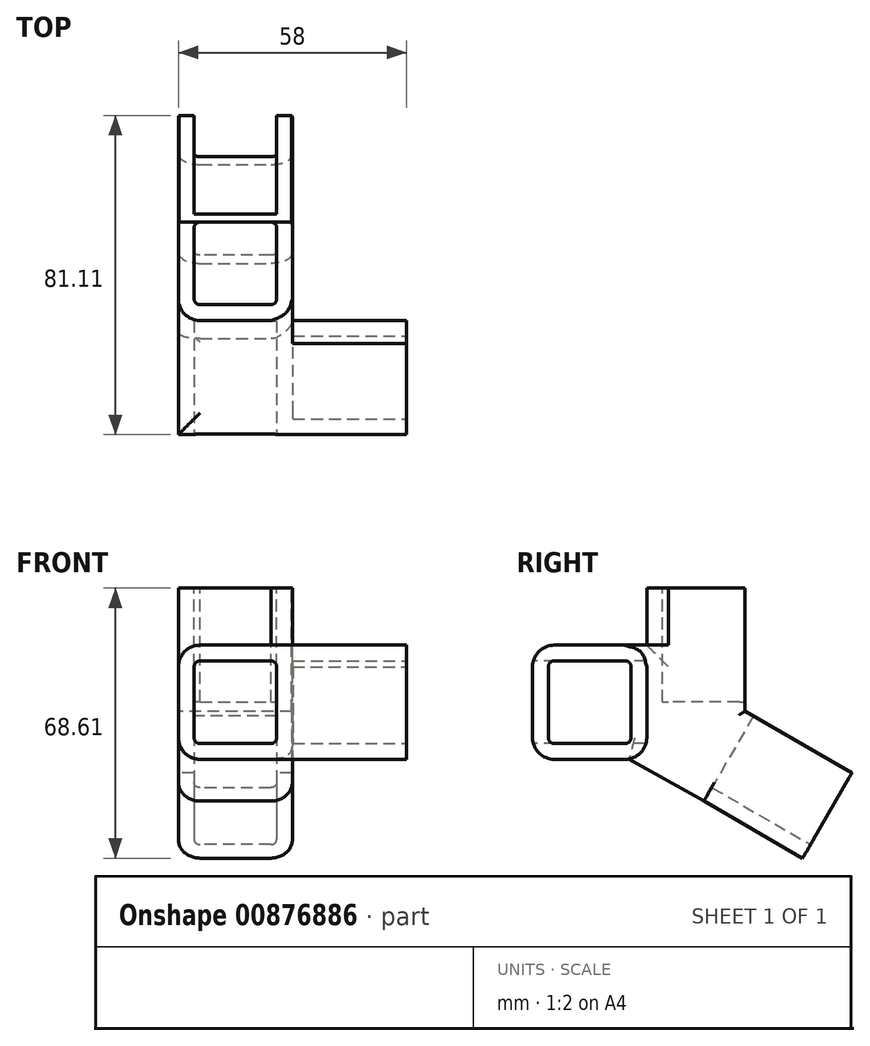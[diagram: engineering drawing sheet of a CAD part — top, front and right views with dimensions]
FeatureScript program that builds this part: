
annotation { "Feature Type Name" : "Feature", "Feature Type Description" : "" }
export const myFeature = defineFeature(function(context is Context, id is Id, definition is map)
    precondition{}
    {
        {
            var Q0;
            Q0=qCreatedBy(makeId("Front.planeOp"),FACE);
            var sketch = newSketch(context, id + "F0", { "sketchPlane" : qUnion([Q0])});
            skLineSegment(sketch, "E0.bottom", {"start": v(-21.09, 20.47) * mm, "end": v(36.91, 20.47) * mm});
            skLineSegment(sketch, "E0.top", {"start": v(-21.09, -8.53) * mm, "end": v(36.91, -8.53) * mm});
            skLineSegment(sketch, "E0.left", {"start": v(-21.09, 20.47) * mm, "end": v(-21.09, -8.53) * mm});
            skLineSegment(sketch, "E0.right", {"start": v(36.91, 20.47) * mm, "end": v(36.91, -8.53) * mm});
            skSolve(sketch);
        }
        {
            var Q0;
            Q0=makeQuery(id+"F0.imprint","IMPRINT",FACE,{"disambiguationData":[TD([[makeQuery(id+"F0.imprint","IMPRINT",EDGE,{"derivedFrom":sQuery(id+"F0.wireOp",EDGE,"E0.bottom")}),-1.0]])]});
            extrude(context, id + "F1", {"entities" : qUnion([Q0]), "depth" : 29 * mm, "offsetDistance" : 25 * mm});
        }
        {
            var Q0;
            Q0=makeQuery(id+"F1.opExtrude","CAP_FACE",FACE,{"disambiguationData":[OSD([sQuery(id+"F0.wireOp",EDGE,"E0.bottom"),sQuery(id+"F0.wireOp",EDGE,"E0.top"),sQuery(id+"F0.wireOp",EDGE,"E0.left"),sQuery(id+"F0.wireOp",EDGE,"E0.right")])],"isStart":false});
            var sketch = newSketch(context, id + "F2", { "sketchPlane" : qUnion([Q0])});
            skLineSegment(sketch, "E1.bottom", {"start": v(-17.09, 16.47) * mm, "end": v(3.91, 16.47) * mm});
            skLineSegment(sketch, "E1.top", {"start": v(-17.09, -4.53) * mm, "end": v(3.91, -4.53) * mm});
            skLineSegment(sketch, "E1.left", {"start": v(-17.09, 16.47) * mm, "end": v(-17.09, -4.53) * mm});
            skLineSegment(sketch, "E1.right", {"start": v(3.91, 16.47) * mm, "end": v(3.91, -4.53) * mm});
            skSolve(sketch);
        }
        {
            var Q0;
            Q0=makeQuery(id+"F2.imprint","IMPRINT",FACE,{"disambiguationData":[TD([[makeQuery(id+"F2.imprint","IMPRINT",EDGE,{"derivedFrom":sQuery(id+"F2.wireOp",EDGE,"E1.bottom")}),-1.0]])]});
            extrude(context, id + "F3", {"entities" : qUnion([Q0]), "operationType" : NewBodyOperationType.REMOVE, "oppositeDirection" : true, "depth" : 28.9 * mm, "offsetDistance" : 25 * mm});
        }
        {
            var Q0;
            Q0=makeQuery(id+"F1.opExtrude","SWEPT_FACE",FACE,{"disambiguationData":[OSD([sQuery(id+"F0.wireOp",EDGE,"E0.right")])]});
            var sketch = newSketch(context, id + "F4", { "sketchPlane" : qUnion([Q0])});
            skLineSegment(sketch, "E2.bottom", {"start": v(-25, 16.47) * mm, "end": v(-4, 16.47) * mm});
            skLineSegment(sketch, "E2.top", {"start": v(-25, -4.53) * mm, "end": v(-4, -4.53) * mm});
            skLineSegment(sketch, "E2.left", {"start": v(-25, 16.47) * mm, "end": v(-25, -4.53) * mm});
            skLineSegment(sketch, "E2.right", {"start": v(-4, 16.47) * mm, "end": v(-4, -4.53) * mm});
            skSolve(sketch);
        }
        {
            var Q0;
            Q0=makeQuery(id+"F4.imprint","IMPRINT",FACE,{"disambiguationData":[TD([[makeQuery(id+"F4.imprint","IMPRINT",EDGE,{"derivedFrom":sQuery(id+"F4.wireOp",EDGE,"E2.bottom")}),-1.0]])]});
            extrude(context, id + "F5", {"entities" : qUnion([Q0]), "operationType" : NewBodyOperationType.REMOVE, "oppositeDirection" : true, "depth" : 28.9 * mm, "offsetDistance" : 25 * mm});
        }
        {
            var Q0;
            Q0=makeQuery(id+"F1.opExtrude","SWEPT_FACE",FACE,{"disambiguationData":[OSD([sQuery(id+"F0.wireOp",EDGE,"E0.bottom")])]});
            var sketch = newSketch(context, id + "F6", { "sketchPlane" : qUnion([Q0])});
            skLineSegment(sketch, "E3.bottom", {"start": v(-21.09, 0) * mm, "end": v(7.91, 0) * mm});
            skLineSegment(sketch, "E3.top", {"start": v(-21.09, 29) * mm, "end": v(7.91, 29) * mm});
            skLineSegment(sketch, "E3.left", {"start": v(-21.09, 0) * mm, "end": v(-21.09, 29) * mm});
            skLineSegment(sketch, "E3.right", {"start": v(7.91, 0) * mm, "end": v(7.91, 29) * mm});
            skSolve(sketch);
        }
        {
            var Q0;
            Q0=makeQuery(id+"F6.imprint","IMPRINT",FACE,{"disambiguationData":[TD([[makeQuery(id+"F6.imprint","IMPRINT",EDGE,{"derivedFrom":sQuery(id+"F6.wireOp",EDGE,"E3.bottom")}),1.0]])]});
            extrude(context, id + "F7", {"entities" : qUnion([Q0]), "operationType" : NewBodyOperationType.ADD, "oppositeDirection" : true, "depth" : 14.5 * mm, "offsetDistance" : 25 * mm});
        }
        {
            var Q0;
            Q0=makeQuery(id+"F7.boolean.opBoolean","MERGE",FACE,{"derivedFrom":[makeQuery(id+"F1.opExtrude","SWEPT_FACE",FACE,{"disambiguationData":[OSD([sQuery(id+"F0.wireOp",EDGE,"E0.bottom")])]}),makeQuery(id+"F7.opExtrude","CAP_FACE",FACE,{"disambiguationData":[OSD([sQuery(id+"F6.wireOp",EDGE,"E3.bottom"),sQuery(id+"F6.wireOp",EDGE,"E3.top"),sQuery(id+"F6.wireOp",EDGE,"E3.left"),sQuery(id+"F6.wireOp",EDGE,"E3.right")])],"isStart":true})]});
            var sketch = newSketch(context, id + "F8", { "sketchPlane" : qUnion([Q0])});
            skLineSegment(sketch, "E4.bottom", {"start": v(-21.09, 29) * mm, "end": v(7.91, 29) * mm});
            skLineSegment(sketch, "E4.top", {"start": v(-21.09, 0) * mm, "end": v(7.91, 0) * mm});
            skLineSegment(sketch, "E4.left", {"start": v(-21.09, 29) * mm, "end": v(-21.09, 0) * mm});
            skLineSegment(sketch, "E4.right", {"start": v(7.91, 29) * mm, "end": v(7.91, 0) * mm});
            skSolve(sketch);
        }
        {
            var Q0;
            Q0=makeQuery(id+"F8.imprint","IMPRINT",FACE,{"disambiguationData":[TD([[makeQuery(id+"F8.imprint","IMPRINT",EDGE,{"derivedFrom":sQuery(id+"F8.wireOp",EDGE,"E4.bottom")}),-1.0]])]});
            extrude(context, id + "F9", {"entities" : qUnion([Q0]), "operationType" : NewBodyOperationType.ADD, "depth" : 14.5 * mm, "offsetDistance" : 25 * mm});
        }
        {
            var Q0;
            Q0=makeQuery(id+"F9.opExtrude","CAP_FACE",FACE,{"disambiguationData":[OSD([sQuery(id+"F8.wireOp",EDGE,"E4.bottom"),sQuery(id+"F8.wireOp",EDGE,"E4.top"),sQuery(id+"F8.wireOp",EDGE,"E4.left"),sQuery(id+"F8.wireOp",EDGE,"E4.right")])],"isStart":false});
            var sketch = newSketch(context, id + "F10", { "sketchPlane" : qUnion([Q0])});
            skLineSegment(sketch, "E5.bottom", {"start": v(-17.09, 25) * mm, "end": v(3.91, 25) * mm});
            skLineSegment(sketch, "E5.top", {"start": v(-17.09, 4) * mm, "end": v(3.91, 4) * mm});
            skLineSegment(sketch, "E5.left", {"start": v(-17.09, 25) * mm, "end": v(-17.09, 4) * mm});
            skLineSegment(sketch, "E5.right", {"start": v(3.91, 25) * mm, "end": v(3.91, 4) * mm});
            skSolve(sketch);
        }
        {
            var Q0;
            Q0=makeQuery(id+"F10.imprint","IMPRINT",FACE,{"disambiguationData":[TD([[makeQuery(id+"F10.imprint","IMPRINT",EDGE,{"derivedFrom":sQuery(id+"F10.wireOp",EDGE,"E5.bottom")}),-1.0]])]});
            extrude(context, id + "F11", {"entities" : qUnion([Q0]), "operationType" : NewBodyOperationType.REMOVE, "oppositeDirection" : true, "depth" : 28.9 * mm, "offsetDistance" : 25 * mm});
        }
        {
            var Q0;
            Q0=makeQuery(id+"F9.boolean.opBoolean","MERGE",FACE,{"derivedFrom":[makeQuery(id+"F7.opExtrude","SWEPT_FACE",FACE,{"disambiguationData":[OSD([sQuery(id+"F6.wireOp",EDGE,"E3.right")])]}),makeQuery(id+"F9.opExtrude","SWEPT_FACE",FACE,{"disambiguationData":[OSD([sQuery(id+"F8.wireOp",EDGE,"E4.right")])]})]});
            var sketch = newSketch(context, id + "F12", { "sketchPlane" : qUnion([Q0])});
            skLineSegment(sketch, "E6", {"start": v(29, 5.97) * mm, "end": v(54.11, -8.53) * mm});
            skLineSegment(sketch, "E7", {"start": v(54.11, -8.53) * mm, "end": v(39.61, -33.64) * mm});
            skLineSegment(sketch, "E8", {"start": v(39.61, -33.64) * mm, "end": v(14.5, -19.14) * mm});
            skLineSegment(sketch, "E9", {"start": v(14.5, -19.14) * mm, "end": v(29, 5.97) * mm});
            skLineSegment(sketch, "E10", {"start": v(14.5, -19.14) * mm, "end": v(-4.5, -8.53) * mm});
            skLineSegment(sketch, "E11", {"start": v(-4.5, -8.53) * mm, "end": v(0, -8.53) * mm});
            skLineSegment(sketch, "E12", {"start": v(0, -8.53) * mm, "end": v(0, 5.97) * mm});
            skLineSegment(sketch, "E13", {"start": v(0, 5.97) * mm, "end": v(29, 5.97) * mm});
            skSolve(sketch);
        }
        {
            var Q0;
            Q0=makeQuery(id+"F12.imprint","IMPRINT",FACE,{"disambiguationData":[TD([[makeQuery(id+"F12.imprint","IMPRINT",EDGE,{"derivedFrom":sQuery(id+"F12.wireOp",EDGE,"E6")}),-1.0]])]});
            var Q1;
            Q1=makeQuery(id+"F12.imprint","IMPRINT",FACE,{"disambiguationData":[TD([[makeQuery(id+"F12.imprint","IMPRINT",EDGE,{"derivedFrom":sQuery(id+"F12.wireOp",EDGE,"E9")}),1.0]])]});
            extrude(context, id + "F13", {"entities" : qUnion([Q0, Q1]), "operationType" : NewBodyOperationType.ADD, "oppositeDirection" : true, "depth" : 29 * mm, "offsetDistance" : 25 * mm});
        }
        {
            var Q0;
            Q0=makeQuery(id+"F13.opExtrude","SWEPT_FACE",FACE,{"disambiguationData":[OSD([sQuery(id+"F12.wireOp",EDGE,"E7")])]});
            var sketch = newSketch(context, id + "F14", { "sketchPlane" : qUnion([Q0])});
            skLineSegment(sketch, "E14.bottom", {"start": v(-3.91, 15.67) * mm, "end": v(17.09, 15.67) * mm});
            skLineSegment(sketch, "E14.top", {"start": v(-3.91, -5.33) * mm, "end": v(17.09, -5.33) * mm});
            skLineSegment(sketch, "E14.left", {"start": v(-3.91, 15.67) * mm, "end": v(-3.91, -5.33) * mm});
            skLineSegment(sketch, "E14.right", {"start": v(17.09, 15.67) * mm, "end": v(17.09, -5.33) * mm});
            skSolve(sketch);
        }
        {
            var Q0;
            Q0=makeQuery(id+"F14.imprint","IMPRINT",FACE,{"disambiguationData":[TD([[makeQuery(id+"F14.imprint","IMPRINT",EDGE,{"derivedFrom":sQuery(id+"F14.wireOp",EDGE,"E14.bottom")}),-1.0]])]});
            extrude(context, id + "F15", {"entities" : qUnion([Q0]), "operationType" : NewBodyOperationType.REMOVE, "oppositeDirection" : true, "depth" : 28.9 * mm, "offsetDistance" : 25 * mm});
        }
        {
            var Q0;
            Q0=makeQuery(id+"F15.boolean.opBoolean","COPY",EDGE,{"derivedFrom":makeQuery(id+"F15.opExtrude","SWEPT_EDGE",EDGE,{"disambiguationData":[OSD([sQuery(id+"F14.wireOp",EDGE,"E14.top"),sQuery(id+"F14.wireOp",EDGE,"E14.left")])]})});
            var Q1;
            Q1=makeQuery(id+"F15.boolean.opBoolean","COPY",EDGE,{"derivedFrom":makeQuery(id+"F15.opExtrude","SWEPT_EDGE",EDGE,{"disambiguationData":[OSD([sQuery(id+"F14.wireOp",EDGE,"E14.top"),sQuery(id+"F14.wireOp",EDGE,"E14.right")])]})});
            var Q2;
            Q2=makeQuery(id+"F11.boolean.opBoolean","COPY",EDGE,{"derivedFrom":makeQuery(id+"F11.opExtrude","SWEPT_EDGE",EDGE,{"disambiguationData":[OSD([sQuery(id+"F10.wireOp",EDGE,"E5.bottom"),sQuery(id+"F10.wireOp",EDGE,"E5.right")])]})});
            var Q3;
            Q3=makeQuery(id+"F11.boolean.opBoolean","COPY",EDGE,{"derivedFrom":makeQuery(id+"F11.opExtrude","SWEPT_EDGE",EDGE,{"disambiguationData":[OSD([sQuery(id+"F10.wireOp",EDGE,"E5.bottom"),sQuery(id+"F10.wireOp",EDGE,"E5.left")])]})});
            var Q4;
            Q4=makeQuery(id+"F11.boolean.opBoolean","COPY",EDGE,{"derivedFrom":makeQuery(id+"F11.opExtrude","SWEPT_EDGE",EDGE,{"disambiguationData":[OSD([sQuery(id+"F10.wireOp",EDGE,"E5.top"),sQuery(id+"F10.wireOp",EDGE,"E5.left")])]})});
            var Q5;
            Q5=makeQuery(id+"F11.boolean.opBoolean","COPY",EDGE,{"derivedFrom":makeQuery(id+"F11.opExtrude","SWEPT_EDGE",EDGE,{"disambiguationData":[OSD([sQuery(id+"F10.wireOp",EDGE,"E5.top"),sQuery(id+"F10.wireOp",EDGE,"E5.right")])]})});
            var Q6;
            Q6=makeQuery(id+"F5.boolean.opBoolean","COPY",EDGE,{"derivedFrom":makeQuery(id+"F5.opExtrude","SWEPT_EDGE",EDGE,{"disambiguationData":[OSD([sQuery(id+"F4.wireOp",EDGE,"E2.top"),sQuery(id+"F4.wireOp",EDGE,"E2.right")])]})});
            var Q7;
            Q7=makeQuery(id+"F5.boolean.opBoolean","COPY",EDGE,{"derivedFrom":makeQuery(id+"F5.opExtrude","SWEPT_EDGE",EDGE,{"disambiguationData":[OSD([sQuery(id+"F4.wireOp",EDGE,"E2.bottom"),sQuery(id+"F4.wireOp",EDGE,"E2.right")])]})});
            var Q8;
            Q8=makeQuery(id+"F5.boolean.opBoolean","COPY",EDGE,{"derivedFrom":makeQuery(id+"F5.opExtrude","SWEPT_EDGE",EDGE,{"disambiguationData":[OSD([sQuery(id+"F4.wireOp",EDGE,"E2.bottom"),sQuery(id+"F4.wireOp",EDGE,"E2.left")])]})});
            var Q9;
            Q9=makeQuery(id+"F5.boolean.opBoolean","COPY",EDGE,{"derivedFrom":makeQuery(id+"F5.opExtrude","SWEPT_EDGE",EDGE,{"disambiguationData":[OSD([sQuery(id+"F4.wireOp",EDGE,"E2.top"),sQuery(id+"F4.wireOp",EDGE,"E2.left")])]})});
            var Q10;
            Q10=makeQuery(id+"F3.boolean.opBoolean","COPY",EDGE,{"derivedFrom":makeQuery(id+"F3.opExtrude","SWEPT_EDGE",EDGE,{"disambiguationData":[OSD([sQuery(id+"F2.wireOp",EDGE,"E1.bottom"),sQuery(id+"F2.wireOp",EDGE,"E1.right")])]})});
            var Q11;
            Q11=makeQuery(id+"F3.boolean.opBoolean","COPY",EDGE,{"derivedFrom":makeQuery(id+"F3.opExtrude","SWEPT_EDGE",EDGE,{"disambiguationData":[OSD([sQuery(id+"F2.wireOp",EDGE,"E1.bottom"),sQuery(id+"F2.wireOp",EDGE,"E1.left")])]})});
            var Q12;
            Q12=makeQuery(id+"F3.boolean.opBoolean","COPY",EDGE,{"derivedFrom":makeQuery(id+"F3.opExtrude","SWEPT_EDGE",EDGE,{"disambiguationData":[OSD([sQuery(id+"F2.wireOp",EDGE,"E1.top"),sQuery(id+"F2.wireOp",EDGE,"E1.left")])]})});
            var Q13;
            Q13=makeQuery(id+"F3.boolean.opBoolean","COPY",EDGE,{"derivedFrom":makeQuery(id+"F3.opExtrude","SWEPT_EDGE",EDGE,{"disambiguationData":[OSD([sQuery(id+"F2.wireOp",EDGE,"E1.top"),sQuery(id+"F2.wireOp",EDGE,"E1.right")])]})});
            fillet(context, id + "F16", {"entities" : qUnion([Q0, Q1, Q2, Q3, Q4, Q5, Q6, Q7, Q8, Q9, Q10, Q11, Q12, Q13]), "radius" : 1.5 * mm, "tangentPropagation" : true, "allowEdgeOverflow" : false});
        }
        {
            var Q0;
            Q0=makeQuery(id+"F9.boolean.opBoolean","MERGE",EDGE,{"derivedFrom":[makeQuery(id+"F7.opExtrude","SWEPT_EDGE",EDGE,{"disambiguationData":[OSD([sQuery(id+"F6.wireOp",EDGE,"E3.top"),sQuery(id+"F6.wireOp",EDGE,"E3.right")])]}),makeQuery(id+"F9.opExtrude","SWEPT_EDGE",EDGE,{"disambiguationData":[OSD([sQuery(id+"F8.wireOp",EDGE,"E4.bottom"),sQuery(id+"F8.wireOp",EDGE,"E4.right")])]})]});
            var Q1;
            Q1=makeQuery(id+"F9.boolean.opBoolean","MERGE",EDGE,{"derivedFrom":[makeQuery(id+"F7.opExtrude","SWEPT_EDGE",EDGE,{"disambiguationData":[OSD([sQuery(id+"F6.wireOp",EDGE,"E3.top"),sQuery(id+"F6.wireOp",EDGE,"E3.left")])]}),makeQuery(id+"F9.opExtrude","SWEPT_EDGE",EDGE,{"disambiguationData":[OSD([sQuery(id+"F8.wireOp",EDGE,"E4.bottom"),sQuery(id+"F8.wireOp",EDGE,"E4.left")])]})]});
            var Q2;
            Q2=makeQuery(id+"F13.opExtrude","CAP_EDGE",EDGE,{"disambiguationData":[OSD([sQuery(id+"F12.wireOp",EDGE,"E6")])],"isStart":false});
            var Q3;
            Q3=makeQuery(id+"F13.opExtrude","CAP_EDGE",EDGE,{"disambiguationData":[OSD([sQuery(id+"F12.wireOp",EDGE,"E6")])],"isStart":true});
            var Q4;
            Q4=makeQuery(id+"F13.opExtrude","CAP_EDGE",EDGE,{"disambiguationData":[OSD([sQuery(id+"F12.wireOp",EDGE,"E8")])],"isStart":false});
            var Q5;
            Q5=makeQuery(id+"F13.opExtrude","CAP_EDGE",EDGE,{"disambiguationData":[OSD([sQuery(id+"F12.wireOp",EDGE,"E8")])],"isStart":true});
            var Q6;
            Q6=makeQuery(id+"F1.opExtrude","SWEPT_EDGE",EDGE,{"disambiguationData":[OSD([sQuery(id+"F0.wireOp",EDGE,"E0.top"),sQuery(id+"F0.wireOp",EDGE,"E0.left")])]});
            var Q7;
            Q7=makeQuery(id+"F7.boolean.opBoolean","MERGE",EDGE,{"derivedFrom":[makeQuery(id+"F1.opExtrude","SWEPT_EDGE",EDGE,{"disambiguationData":[OSD([sQuery(id+"F0.wireOp",EDGE,"E0.bottom"),sQuery(id+"F0.wireOp",EDGE,"E0.left")])]}),makeQuery(id+"F7.opExtrude","CAP_EDGE",EDGE,{"disambiguationData":[OSD([sQuery(id+"F6.wireOp",EDGE,"E3.left")])],"isStart":true})]});
            var Q8;
            Q8=makeQuery(id+"F9.opExtrude","SWEPT_EDGE",EDGE,{"disambiguationData":[OSD([sQuery(id+"F0.wireOp",EDGE,"E0.bottom"),sQuery(id+"F0.wireOp",EDGE,"E0.left"),sQuery(id+"F6.wireOp",EDGE,"E3.left"),sQuery(id+"F8.wireOp",EDGE,"E4.top"),sQuery(id+"F8.wireOp",EDGE,"E4.left")])]});
            var Q9;
            Q9=makeQuery(id+"F1.opExtrude","CAP_EDGE",EDGE,{"disambiguationData":[OSD([sQuery(id+"F0.wireOp",EDGE,"E0.bottom")])],"isStart":false});
            var Q10;
            Q10=makeQuery(id+"F1.opExtrude","CAP_EDGE",EDGE,{"disambiguationData":[OSD([sQuery(id+"F0.wireOp",EDGE,"E0.top")])],"isStart":false});
            fillet(context, id + "F17", {"entities" : qUnion([Q0, Q1, Q2, Q3, Q4, Q5, Q6, Q7, Q8, Q9, Q10]), "radius" : 5.5 * mm, "tangentPropagation" : true, "allowEdgeOverflow" : false});
        }
        {
            var Q0;
            Q0=makeQuery(id+"F1.opExtrude","CAP_EDGE",EDGE,{"disambiguationData":[OSD([sQuery(id+"F0.wireOp",EDGE,"E0.top")])],"isStart":true});
            fillet(context, id + "F18", {"entities" : qUnion([Q0]), "radius" : 5.5 * mm, "tangentPropagation" : true, "allowEdgeOverflow" : false});
        }
        {
            var Q0;
            Q0=makeQuery(id+"F1.opExtrude","SWEPT_FACE",FACE,{"disambiguationData":[OSD([sQuery(id+"F0.wireOp",EDGE,"E0.right")])]});
            var sketch = newSketch(context, id + "F19", { "sketchPlane" : qUnion([Q0])});
            skFitSpline(sketch, "E15", {"points": [v(0, 14.97) * mm, v(-1.56, 18.78) * mm, v(-5.9, 20.47) * mm], "startDerivative": vector(-1.97, 8.97) * mm, "endDerivative": vector(-9.75, 2.1) * mm});
            skLineSegment(sketch, "E16", {"start": v(-5.9, 20.47) * mm, "end": v(-5.9, 16.47) * mm});
            skLineSegment(sketch, "E17", {"start": v(-5.9, 16.47) * mm, "end": v(-5.5, 16.47) * mm});
            skLineSegment(sketch, "E18", {"start": v(0, 14.97) * mm, "end": v(-4, 14.97) * mm});
            skSolve(sketch);
        }
        {
            var Q0;
            {var subQ0=sQuery(id+"F19.wireOp",EDGE,"E15");Q0=makeQuery(id+"F19.imprint","IMPRINT",FACE,{"disambiguationData":[TD([[makeQuery(id+"F19.imprint","IMPRINT",EDGE,{"derivedFrom":subQ0}),-1.0]])]});}
            extrude(context, id + "F20", {"entities" : qUnion([Q0]), "operationType" : NewBodyOperationType.REMOVE, "oppositeDirection" : true, "depth" : 29 * mm, "offsetDistance" : 25 * mm});
        }
        {
            var Q0;
            Q0=makeQuery(id+"F9.opExtrude","CAP_FACE",FACE,{"disambiguationData":[OSD([sQuery(id+"F8.wireOp",EDGE,"E4.bottom"),sQuery(id+"F8.wireOp",EDGE,"E4.top"),sQuery(id+"F8.wireOp",EDGE,"E4.left"),sQuery(id+"F8.wireOp",EDGE,"E4.right")])],"isStart":false});
            var sketch = newSketch(context, id + "F21", { "sketchPlane" : qUnion([Q0])});
            skFitSpline(sketch, "E19", {"points": [v(7.91, 5.5) * mm, v(6.27, 1.96) * mm, v(2.44, 0) * mm], "startDerivative": vector(-2.37, -8.1) * mm, "endDerivative": vector(-8.54, -2.94) * mm});
            skSolve(sketch);
        }
        {
            var Q0;
            {var subQ0=sQuery(id+"F21.wireOp",EDGE,"E19");Q0=makeQuery(id+"F21.imprint","IMPRINT",FACE,{"disambiguationData":[TD([[makeQuery(id+"F21.imprint","IMPRINT",EDGE,{"derivedFrom":subQ0}),1.0]])]});}
            extrude(context, id + "F22", {"entities" : qUnion([Q0]), "operationType" : NewBodyOperationType.REMOVE, "oppositeDirection" : true, "depth" : 14.5 * mm, "offsetDistance" : 25 * mm});
        }
        {
            var Q0;
            Q0=makeQuery(id+"F9.opExtrude","CAP_FACE",FACE,{"disambiguationData":[OSD([sQuery(id+"F8.wireOp",EDGE,"E4.bottom"),sQuery(id+"F8.wireOp",EDGE,"E4.top"),sQuery(id+"F8.wireOp",EDGE,"E4.left"),sQuery(id+"F8.wireOp",EDGE,"E4.right")])],"isStart":false});
            var sketch = newSketch(context, id + "F23", { "sketchPlane" : qUnion([Q0])});
            skLineSegment(sketch, "E20", {"start": v(-15.59, 25) * mm, "end": v(-31.91, 25) * mm});
            skLineSegment(sketch, "E21", {"start": v(-31.91, 25) * mm, "end": v(-31.91, 34.16) * mm});
            skLineSegment(sketch, "E22", {"start": v(-31.91, 34.16) * mm, "end": v(16, 34.16) * mm});
            skLineSegment(sketch, "E23", {"start": v(16, 34.16) * mm, "end": v(16, 25) * mm});
            skLineSegment(sketch, "E24", {"start": v(16, 25) * mm, "end": v(-15.59, 25) * mm});
            skSolve(sketch);
        }
        {
            var Q0;
            {var subQ4=sQuery(id+"F8.wireOp",EDGE,"E4.bottom");var subQ9=makeQuery(id+"F9.opExtrude","CAP_EDGE",EDGE,{"disambiguationData":[OSD([subQ4])],"isStart":false});Q0=makeQuery(id+"F23.imprint","IMPRINT",FACE,{"disambiguationData":[TD([[makeQuery(id+"F23.imprint","IMPRINT",EDGE,{"derivedFrom":subQ9}),-1.0]])]});}
            extrude(context, id + "F24", {"entities" : qUnion([Q0]), "operationType" : NewBodyOperationType.REMOVE, "oppositeDirection" : true, "depth" : 31.3 * mm, "offsetDistance" : 25 * mm});
        }
        {
            var Q0;
            Q0=makeQuery(id+"F13.opExtrude","SWEPT_FACE",FACE,{"disambiguationData":[OSD([sQuery(id+"F12.wireOp",EDGE,"E7")])]});
            var sketch = newSketch(context, id + "F25", { "sketchPlane" : qUnion([Q0])});
            skLineSegment(sketch, "E25", {"start": v(17.09, 15.67) * mm, "end": v(25.46, 15.67) * mm});
            skLineSegment(sketch, "E26", {"start": v(25.46, 15.67) * mm, "end": v(25.46, 22.99) * mm});
            skLineSegment(sketch, "E27", {"start": v(25.46, 22.99) * mm, "end": v(-10.08, 22.99) * mm});
            skLineSegment(sketch, "E28", {"start": v(-10.08, 22.99) * mm, "end": v(-11, 15.67) * mm});
            skLineSegment(sketch, "E29", {"start": v(-11, 15.67) * mm, "end": v(17.09, 15.67) * mm});
            skSolve(sketch);
        }
        {
            var Q0;
            {var subQ0=sQuery(id+"F12.wireOp",EDGE,"E7");var subQ1=sQuery(id+"F12.wireOp",EDGE,"E6");var subQ2=makeQuery(id+"F13.opExtrude","SWEPT_EDGE",EDGE,{"disambiguationData":[OSD([subQ1,subQ0])]});Q0=makeQuery(id+"F25.imprint","IMPRINT",FACE,{"disambiguationData":[TD([[makeQuery(id+"F25.imprint","IMPRINT",EDGE,{"derivedFrom":subQ2}),1.0]])]});}
            extrude(context, id + "F26", {"entities" : qUnion([Q0]), "operationType" : NewBodyOperationType.REMOVE, "oppositeDirection" : true, "depth" : 31.3 * mm, "offsetDistance" : 25 * mm});
        }
    });
